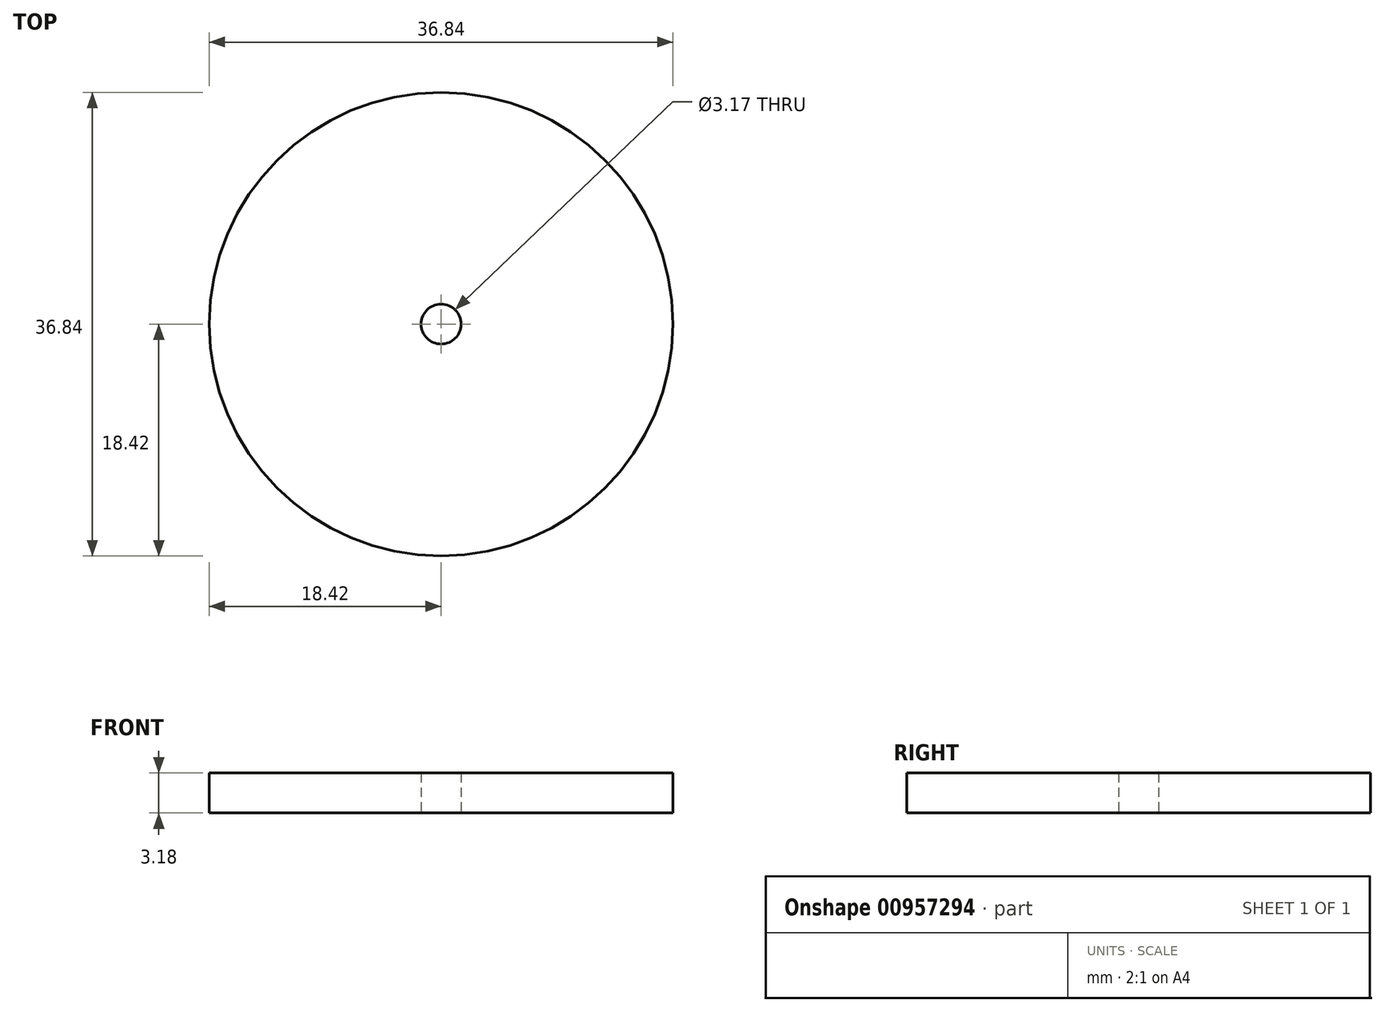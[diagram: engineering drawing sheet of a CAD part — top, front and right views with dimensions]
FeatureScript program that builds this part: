
annotation { "Feature Type Name" : "Feature", "Feature Type Description" : "" }
export const myFeature = defineFeature(function(context is Context, id is Id, definition is map)
    precondition{}
    {
        {
            var Q0;
            Q0=qCreatedBy(makeId("Top.planeOp"),FACE);
            var sketch = newSketch(context, id + "F0", { "sketchPlane" : qUnion([Q0])});
            skCircle(sketch, "E0", {"center": v(0, 0) * mm, "radius": 18.41 * mm});
            skCircle(sketch, "E1", {"center": v(0, 0) * mm, "radius": 1.59 * mm});
            skSolve(sketch);
        }
        {
            var Q0;
            Q0 = qSketchRegion(id + "F0", true);
            extrude(context, id + "F1", {"entities" : qUnion([Q0]), "depth" : 3.17 * mm, "offsetDistance" : 25.4 * mm});
        }
    });
